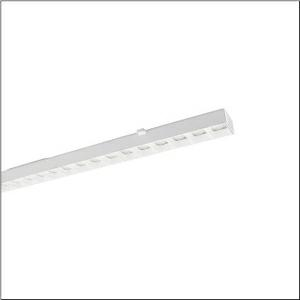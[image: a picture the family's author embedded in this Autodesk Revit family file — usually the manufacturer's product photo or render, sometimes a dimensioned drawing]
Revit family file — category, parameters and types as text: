
# Revit family: silica_31_fur_modario_31_51ry19mb46c
name_source: partatom
category: Lighting Fixtures
units: mm (PartAtom-declared; Revit-internal decimal feet)

## family parameters
Cut with Voids When Loaded = No
Host = Face
Light Source = No
Part Type = Normal
Room Calculation Point = No
Round Connector Dimension = Use Diameter
Shared = No

## types (1)
- --- (1 x LED, 6620 lm, 37.8 W, 4000K)
    Apparent Load = 38 VA
    CIE Flux Codes = 72 95 99 100 100
    Color Rendering = 80
    Color Temperature = 4000K
    Default Elevation = 1800 mm
    Description = Silica 31 for Modario 31, luminaire insert, of aluminium, coated, traffic white (RAL 9016), length: 1.495mm, width: 79mm, height: 62mm, 5x system unit, system units: 299mm, LED rated luminous flux: 6.620lm, light colour: 840, SDCM (Standard Deviation of Colour Matching)MacAdam ≤ 3 SDCM (initial), control gear: ON/OFF Multilumen, with system connector: socket, mains connection: 220..240V, AC, 50/60Hz, rated input power: 38W, luminous flux adjustable on luminaire in four steps (3850/4650/5610/6620lm), connected load according to luminous flux setting (21.7/26.2/31.8/37.8W), primary light control with lens, of PMMA, primary anti-glare with reflector, of PC, light emission: direct distribution, primary light characteristic: double asymmetric, protection rating (complete): IP20, insulation class (complete): insulation class I (protective earthing), certification: CE, UKCA, impact resistance: IK02, permissible ambient temperature for indoor applications: -20..+40°C, packaging unit: 1 piece
    Height = 62 mm
    Lamp = 1 x LED
    Lamp Light Flux = 6620 lm
    Lamp Power = 37.8 W
    Lamp count = 1
    Length = 1495 mm
    Luminous efficacy = 175 lm/W
    Manufacturer = Siteco
    ModVariant = No
    Model = 51RY19MB46C
    Mounting Place = Ceiling
    Mounting Type = Pendant
    Number of Poles = 1
    OnlyDefault = Yes
    Power Factor = 1
    Product Name = Silica 31 für Modario 31
    Product group = luminaire insert | ceiling pendant
    ProductGroupID = 901
    Protection Class = Protection class I
    Protection Degree = IP 20
    RLX_Detail_Level = 1
    RLX_Emergency_Light_Flux = 0 lm
    RLX_Emergency_Type = 0
    RLX_Emergency_Type_DB = No
    RlxData = <blob elided: 14105 chars, md5=2130cee9>
    Socket = socket
    Standby Power = 0 W
    System Light Flux = 6620 lm
    System Power = 38 W
    Type Comments = factory setting: luminous flux: 100 % | (OFF | OFF | OFF) | 350 mA
    Type Image = l_1299352.jpg
    URL = http://relux.com
    VarID = @adj_064645
    Voltage = 0 V
    Weight = 0.00 kg
    Width = 79 mm

## geometry (parser evidence)
native form markers: Sweep x10
no freeform markers — native parametric forms only
